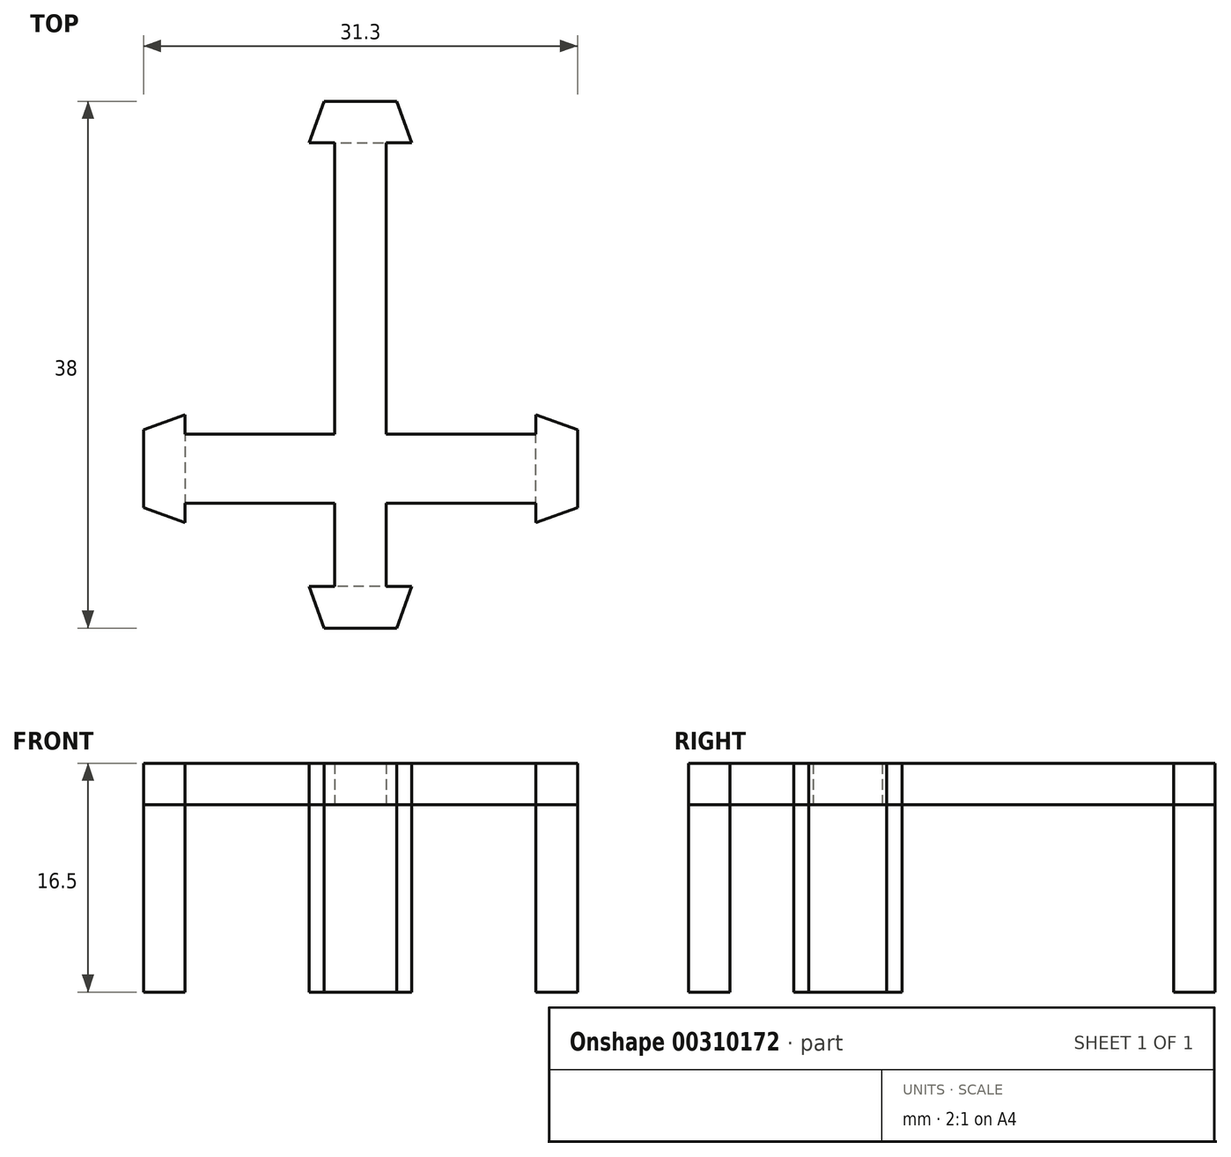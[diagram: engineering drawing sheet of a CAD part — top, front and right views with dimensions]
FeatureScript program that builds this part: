
annotation { "Feature Type Name" : "Feature", "Feature Type Description" : "" }
export const myFeature = defineFeature(function(context is Context, id is Id, definition is map)
    precondition{}
    {
        {
            var Q0;
            Q0=qCreatedBy(makeId("Top.planeOp"),FACE);
            var sketch = newSketch(context, id + "F0", { "sketchPlane" : qUnion([Q0])});
            skLineSegment(sketch, "E0", {"start": v(0, 16.06) * mm, "end": v(0, -15.94) * mm, "construction": true});
            skLineSegment(sketch, "E1", {"start": v(0, 16.06) * mm, "end": v(3.7, 16.06) * mm});
            skLineSegment(sketch, "E2", {"start": v(0, 16.06) * mm, "end": v(-3.7, 16.06) * mm});
            skLineSegment(sketch, "E3", {"start": v(0, -15.94) * mm, "end": v(-3.7, -15.94) * mm});
            skLineSegment(sketch, "E4", {"start": v(0, -15.94) * mm, "end": v(3.7, -15.94) * mm});
            skLineSegment(sketch, "E5", {"start": v(12.65, -7.44) * mm, "end": v(12.65, -4.94) * mm});
            skLineSegment(sketch, "E6", {"start": v(12.65, -7.44) * mm, "end": v(12.65, -9.94) * mm});
            skLineSegment(sketch, "E7", {"start": v(12.65, -11.34) * mm, "end": v(15.65, -10.25) * mm});
            skLineSegment(sketch, "E8", {"start": v(15.65, -10.25) * mm, "end": v(15.65, -4.63) * mm});
            skLineSegment(sketch, "E9", {"start": v(15.65, -4.63) * mm, "end": v(12.65, -3.54) * mm});
            skLineSegment(sketch, "E10", {"start": v(12.65, -4.94) * mm, "end": v(12.65, -3.54) * mm});
            skLineSegment(sketch, "E11", {"start": v(12.65, -9.94) * mm, "end": v(12.65, -11.34) * mm});
            skLineSegment(sketch, "E12", {"start": v(12.65, -4.94) * mm, "end": v(3.7, -4.94) * mm});
            skLineSegment(sketch, "E13", {"start": v(12.65, -9.94) * mm, "end": v(1.85, -9.94) * mm});
            skLineSegment(sketch, "E14.MirrorCS", {"start": v(-15.65, -4.63) * mm, "end": v(-12.65, -3.54) * mm});
            skLineSegment(sketch, "E15.MirrorCS", {"start": v(-12.65, -9.94) * mm, "end": v(-12.65, -11.34) * mm});
            skLineSegment(sketch, "E16.MirrorCS", {"start": v(-12.65, -9.94) * mm, "end": v(-3.7, -9.94) * mm});
            skLineSegment(sketch, "E17.MirrorCS", {"start": v(-12.65, -7.44) * mm, "end": v(-12.65, -9.94) * mm});
            skLineSegment(sketch, "E18.MirrorCS", {"start": v(-12.65, -11.34) * mm, "end": v(-15.65, -10.25) * mm});
            skLineSegment(sketch, "E19.MirrorCS", {"start": v(-15.65, -10.25) * mm, "end": v(-15.65, -4.63) * mm});
            skLineSegment(sketch, "E20.MirrorCS", {"start": v(-12.65, -4.94) * mm, "end": v(-12.65, -3.54) * mm});
            skLineSegment(sketch, "E21.MirrorCS", {"start": v(-12.65, -7.44) * mm, "end": v(-12.65, -4.94) * mm});
            skLineSegment(sketch, "E22.MirrorCS", {"start": v(-12.65, -4.94) * mm, "end": v(-3.7, -4.94) * mm});
            skLineSegment(sketch, "E23", {"start": v(-3.7, -9.94) * mm, "end": v(-1.85, -9.94) * mm});
            skLineSegment(sketch, "E24", {"start": v(-3.7, -4.94) * mm, "end": v(-1.85, -4.94) * mm});
            skLineSegment(sketch, "E25", {"start": v(3.7, -4.94) * mm, "end": v(1.85, -4.94) * mm});
            skLineSegment(sketch, "E26", {"start": v(-3.7, -15.94) * mm, "end": v(-2.6, -18.94) * mm});
            skLineSegment(sketch, "E27", {"start": v(-2.6, -18.94) * mm, "end": v(2.6, -18.94) * mm});
            skLineSegment(sketch, "E28", {"start": v(2.6, -18.94) * mm, "end": v(3.7, -15.94) * mm});
            skLineSegment(sketch, "E29", {"start": v(1.85, -15.94) * mm, "end": v(1.85, -9.94) * mm});
            skLineSegment(sketch, "E30", {"start": v(-1.85, -15.94) * mm, "end": v(-1.85, -9.94) * mm});
            skLineSegment(sketch, "E31", {"start": v(1.85, -9.94) * mm, "end": v(1.85, -9.94) * mm});
            skLineSegment(sketch, "E32", {"start": v(-3.7, 16.06) * mm, "end": v(-2.6, 19.06) * mm});
            skLineSegment(sketch, "E33", {"start": v(-2.6, 19.06) * mm, "end": v(2.6, 19.06) * mm});
            skLineSegment(sketch, "E34", {"start": v(2.6, 19.06) * mm, "end": v(3.7, 16.06) * mm});
            skLineSegment(sketch, "E35", {"start": v(-1.85, 16.06) * mm, "end": v(-1.85, -4.94) * mm});
            skLineSegment(sketch, "E36", {"start": v(1.85, -4.94) * mm, "end": v(1.85, 16.06) * mm});
            skSolve(sketch);
        }
        {
            var Q0;
            Q0=makeQuery(id+"F0.imprint","IMPRINT",FACE,{"disambiguationData":[TD([[makeQuery(id+"F0.imprint","IMPRINT",EDGE,{"derivedFrom":sQuery(id+"F0.wireOp",EDGE,"E5")}),-1.0]])]});
            var Q1;
            Q1=makeQuery(id+"F0.imprint","IMPRINT",FACE,{"disambiguationData":[TD([[makeQuery(id+"F0.imprint","IMPRINT",EDGE,{"derivedFrom":sQuery(id+"F0.wireOp",EDGE,"E14.MirrorCS")}),-1.0]])]});
            var Q2;
            {var subQ3=sQuery(id+"F0.wireOp",EDGE,"E26");Q2=makeQuery(id+"F0.imprint","IMPRINT",FACE,{"disambiguationData":[TD([[makeQuery(id+"F0.imprint","IMPRINT",EDGE,{"derivedFrom":subQ3}),1.0]])]});}
            var Q3;
            {var subQ0=sQuery(id+"F0.wireOp",EDGE,"E32");Q3=makeQuery(id+"F0.imprint","IMPRINT",FACE,{"disambiguationData":[TD([[makeQuery(id+"F0.imprint","IMPRINT",EDGE,{"derivedFrom":subQ0}),-1.0]])]});}
            extrude(context, id + "F1", {"entities" : qUnion([Q0, Q1, Q2, Q3]), "depth" : -13.5 * mm});
        }
        {
            var Q0;
            Q0 = qSketchRegion(id + "F0", true);
            extrude(context, id + "F2", {"entities" : qUnion([Q0]), "depth" : 3 * mm});
        }
    });
